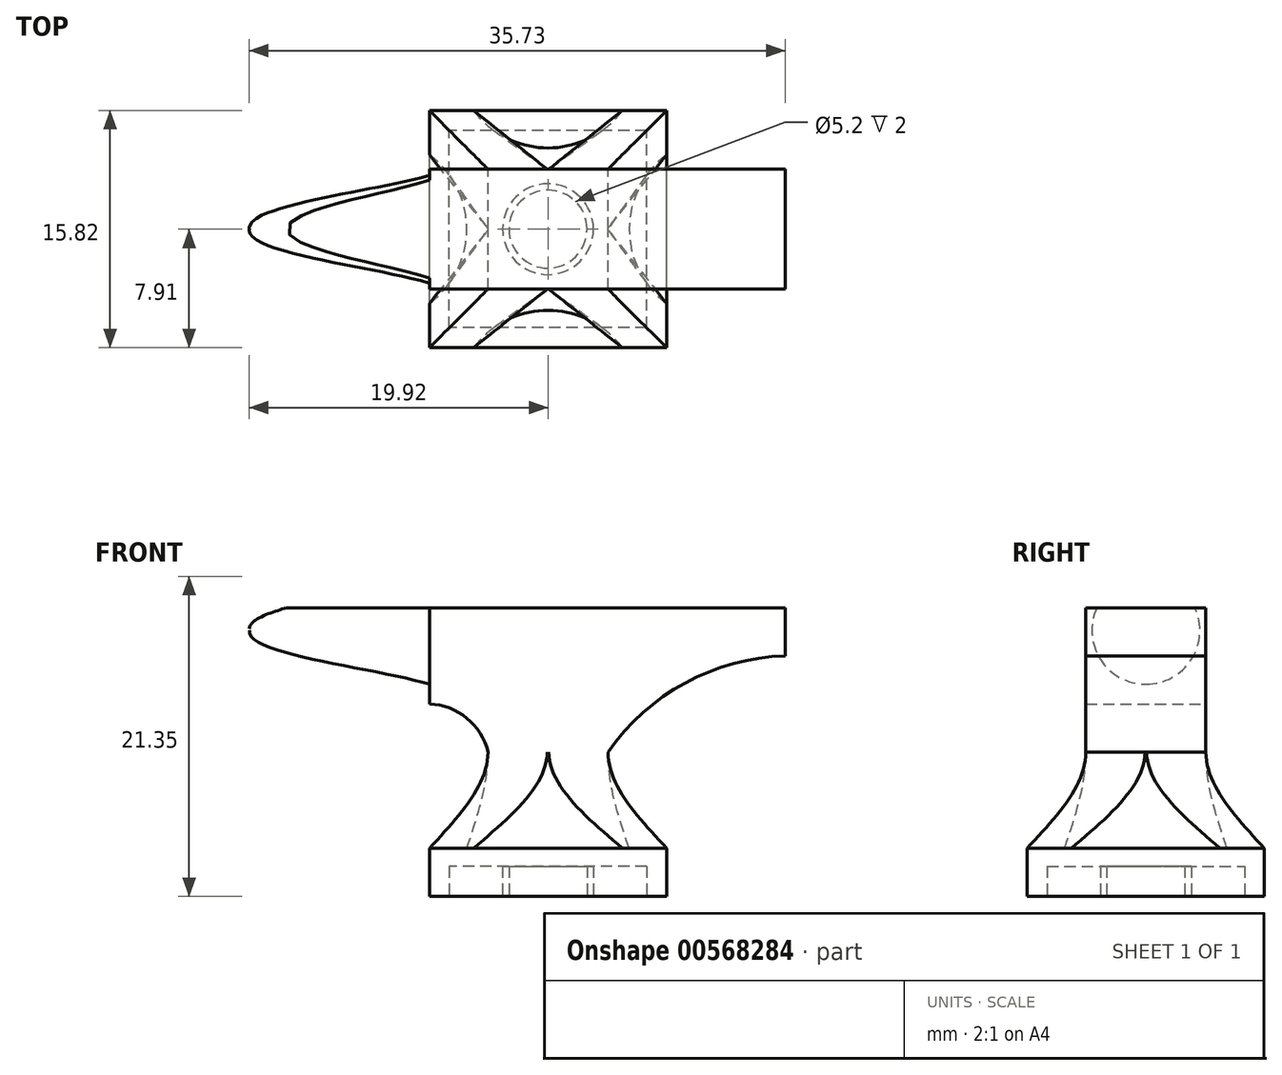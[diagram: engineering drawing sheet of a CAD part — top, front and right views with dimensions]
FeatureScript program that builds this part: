
annotation { "Feature Type Name" : "Feature", "Feature Type Description" : "" }
export const myFeature = defineFeature(function(context is Context, id is Id, definition is map)
    precondition{}
    {
        {
            assignVariable(context, id + "F0", {"name" : "lego_standard_width", "anyValue" : 15.8 / 2});
        }
        {
            assignVariable(context, id + "F1", {"name" : "base_width", "anyValue" : 8});
        }
        {
            var Q0;
            Q0=qCreatedBy(makeId("Front.planeOp"),FACE);
            var sketch = newSketch(context, id + "F2", { "sketchPlane" : qUnion([Q0])});
            skLineSegment(sketch, "E0", {"start": v(-7.9, 12.83) * mm, "end": v(-7.9, 19.25) * mm});
            skLineSegment(sketch, "E1", {"start": v(-7.9, 19.25) * mm, "end": v(15.8, 19.25) * mm});
            skLineSegment(sketch, "E2", {"start": v(15.8, 19.25) * mm, "end": v(15.8, 16.04) * mm});
            skLineSegment(sketch, "E3", {"start": v(-4, 9.62) * mm, "end": v(4, 9.62) * mm});
            skArc(sketch, "E4", {"start": v(-4, 9.62) * mm, "mid": v(-5.41, 11.89) * mm, "end": v(-7.9, 12.83) * mm});
            skArc(sketch, "E5", {"start": v(15.8, 16.04) * mm, "mid": v(9.14, 14.23) * mm, "end": v(4, 9.62) * mm});
            skLineSegment(sketch, "E6.bottom", {"start": v(7.9, 0) * mm, "end": v(-7.9, 0) * mm});
            skLineSegment(sketch, "E6.top", {"start": v(7.9, 3.21) * mm, "end": v(-7.9, 3.2) * mm});
            skLineSegment(sketch, "E6.left", {"start": v(7.9, 0) * mm, "end": v(7.9, 3.2) * mm});
            skLineSegment(sketch, "E6.right", {"start": v(-7.9, 0) * mm, "end": v(-7.9, 3.2) * mm});
            skPoint(sketch, "E6.middle", {"position": v(0, 1.6) * mm});
            skLineSegment(sketch, "E7", {"start": v(0, 3.2) * mm, "end": v(0, 9.62) * mm, "construction": true});
            skLineSegment(sketch, "E8", {"start": v(-7.9, 3.2) * mm, "end": v(-7.9, 12.83) * mm, "construction": true});
            skSolve(sketch);
        }
        {
            var Q0;
            Q0=makeQuery(id+"F2.imprint","IMPRINT",FACE,{"disambiguationData":[TD([[makeQuery(id+"F2.imprint","IMPRINT",EDGE,{"derivedFrom":sQuery(id+"F2.wireOp",EDGE,"E6.bottom")}),-1.0]])]});
            extrude(context, id + "F3", {"entities" : qUnion([Q0]), "depth" : getVariable(context, 'lego_standard_width') * mm, "offsetDistance" : 25 * mm, "hasSecondDirection" : true, "secondDirectionOppositeDirection" : true, "secondDirectionDepth" : getVariable(context, 'lego_standard_width') * mm});
        }
        {
            var Q0;
            Q0=makeQuery(id+"F2.imprint","IMPRINT",FACE,{"disambiguationData":[TD([[makeQuery(id+"F2.imprint","IMPRINT",EDGE,{"derivedFrom":sQuery(id+"F2.wireOp",EDGE,"E0")}),-1.0]])]});
            extrude(context, id + "F4", {"entities" : qUnion([Q0]), "depth" : getVariable(context, 'base_width') / 2 * mm, "offsetDistance" : 25 * mm, "hasSecondDirection" : true, "secondDirectionOppositeDirection" : true, "secondDirectionDepth" : getVariable(context, 'base_width') / 2 * mm});
        }
        {
            var Q0;
            Q0=makeQuery(id+"F3.opExtrude","SWEPT_FACE",FACE,{"disambiguationData":[OSD([sQuery(id+"F2.wireOp",EDGE,"E6.top")])]});
            var sketch = newSketch(context, id + "F5", { "sketchPlane" : qUnion([Q0])});
            skLineSegment(sketch, "E9", {"start": v(-7.9, 7.9) * mm, "end": v(7.9, -7.9) * mm, "construction": true});
            skLineSegment(sketch, "E10", {"start": v(-7.9, -7.9) * mm, "end": v(7.9, 7.9) * mm, "construction": true});
            skLineSegment(sketch, "E11", {"start": v(7.9, 7.9) * mm, "end": v(4.95, 7.9) * mm});
            skLineSegment(sketch, "E12", {"start": v(7.9, 7.9) * mm, "end": v(7.9, 4.95) * mm});
            skArc(sketch, "E13", {"start": v(7.9, 4.95) * mm, "mid": v(5.42, 0) * mm, "end": v(7.9, -4.95) * mm});
            skLineSegment(sketch, "E14.1.0", {"start": v(-7.9, 7.9) * mm, "end": v(-4.95, 7.9) * mm});
            skArc(sketch, "E14.1.1", {"start": v(-4.95, 7.9) * mm, "mid": v(0, 5.42) * mm, "end": v(4.95, 7.9) * mm});
            skLineSegment(sketch, "E14.1.2", {"start": v(-7.9, 7.9) * mm, "end": v(-7.9, 4.95) * mm});
            skLineSegment(sketch, "E14.2.0", {"start": v(-7.9, -7.9) * mm, "end": v(-7.9, -4.95) * mm});
            skArc(sketch, "E14.2.1", {"start": v(-7.9, -4.95) * mm, "mid": v(-5.42, 0) * mm, "end": v(-7.9, 4.95) * mm});
            skLineSegment(sketch, "E14.2.2", {"start": v(-7.9, -7.9) * mm, "end": v(-4.95, -7.9) * mm});
            skLineSegment(sketch, "E14.3.0", {"start": v(7.9, -7.9) * mm, "end": v(4.95, -7.9) * mm});
            skArc(sketch, "E14.3.1", {"start": v(4.95, -7.9) * mm, "mid": v(0, -5.42) * mm, "end": v(-4.95, -7.9) * mm});
            skLineSegment(sketch, "E14.3.2", {"start": v(7.9, -7.9) * mm, "end": v(7.9, -4.95) * mm});
            skPoint(sketch, "E14.center", {"position": v(0, 0) * mm});
            skSolve(sketch);
        }
        {
            var Q0;
            Q0=makeQuery(id+"F4.opExtrude","SWEPT_FACE",FACE,{"disambiguationData":[OSD([sQuery(id+"F2.wireOp",EDGE,"E3")])]});
            var sketch = newSketch(context, id + "F6", { "sketchPlane" : qUnion([Q0])});
            skLineSegment(sketch, "E15", {"start": v(-4, 4) * mm, "end": v(-0.05, 4) * mm});
            skLineSegment(sketch, "E16", {"start": v(-0.05, 4) * mm, "end": v(0.05, 4) * mm});
            skLineSegment(sketch, "E17", {"start": v(0.05, 4) * mm, "end": v(4, 4) * mm});
            skLineSegment(sketch, "E18", {"start": v(4, 4) * mm, "end": v(4, 0.05) * mm});
            skLineSegment(sketch, "E19", {"start": v(4, 0.05) * mm, "end": v(4, -0.05) * mm});
            skLineSegment(sketch, "E20", {"start": v(4, -0.05) * mm, "end": v(4, -4) * mm});
            skLineSegment(sketch, "E21", {"start": v(4, -4) * mm, "end": v(0.05, -4) * mm});
            skLineSegment(sketch, "E22", {"start": v(0.05, -4) * mm, "end": v(-0.05, -4) * mm});
            skLineSegment(sketch, "E23", {"start": v(-0.05, -4) * mm, "end": v(-4, -4) * mm});
            skLineSegment(sketch, "E24", {"start": v(-4, -4) * mm, "end": v(-4, -0.05) * mm});
            skLineSegment(sketch, "E25", {"start": v(-4, -0.05) * mm, "end": v(-4, 0.05) * mm});
            skLineSegment(sketch, "E26", {"start": v(-4, 0.05) * mm, "end": v(-4, 4) * mm});
            skPoint(sketch, "E27", {"position": v(0, 4) * mm});
            skSolve(sketch);
        }
        {
            var Q2;
            Q2=makeQuery(id+"F6.imprint","IMPRINT",FACE,{"disambiguationData":[TD([[makeQuery(id+"F6.imprint","IMPRINT",EDGE,{"derivedFrom":sQuery(id+"F6.wireOp",EDGE,"E15")}),-1.0]])]});
            var Q3;
            Q3=makeQuery(id+"F5.imprint","IMPRINT",FACE,{"disambiguationData":[TD([[makeQuery(id+"F5.imprint","IMPRINT",EDGE,{"derivedFrom":sQuery(id+"F5.wireOp",EDGE,"E11")}),1.0]])]});
            loft(context, id + "F7", {"operationType" : NewBodyOperationType.ADD, "startCondition" : LoftEndDerivativeType.NORMAL_TO_PROFILE, "startMagnitude" : 1, "sheetProfilesArray" : [{ "sheetProfileEntities" : qUnion([Q2]) }, { "sheetProfileEntities" : qUnion([Q3]) }]});
        }
        {
            var Q0;
            Q0=qCreatedBy(makeId("Front.planeOp"),FACE);
            var sketch = newSketch(context, id + "F8", { "sketchPlane" : qUnion([Q0])});
            skLineSegment(sketch, "E28.0", {"start": v(-7.9, 12.83) * mm, "end": v(-7.9, 19.25) * mm});
            skLineSegment(sketch, "E29", {"start": v(-7.9, 17.75) * mm, "end": v(-19.9, 17.75) * mm});
            skFitSpline(sketch, "E30", {"points": [v(-19.9, 17.75) * mm, v(-7.9, 14.15) * mm], "startDerivative": vector(-1.13, -4.8) * mm, "endDerivative": vector(10.6, -3.2) * mm});
            skSolve(sketch);
        }
        {
            var Q0;
            {var subQ0=sQuery(id+"F8.wireOp",EDGE,"E29");Q0=makeQuery(id+"F8.imprint","IMPRINT",FACE,{"disambiguationData":[TD([[makeQuery(id+"F8.imprint","IMPRINT",EDGE,{"derivedFrom":subQ0}),1.0]])]});}
            var Q1;
            Q1=sQuery(id+"F8.wireOp",EDGE,"E30");
            var Q2;
            Q2=sQuery(id+"F8.wireOp",EDGE,"E29");
            revolve(context, id + "F9", {"operationType" : NewBodyOperationType.ADD, "entities" : qUnion([Q0]), "surfaceEntities" : qUnion([Q1]), "axis" : qUnion([Q2]), "revolveType" : RevolveType.FULL});
        }
        {
            var Q0;
            Q0=makeQuery(id+"F9.opRevolve","SWEPT_FACE",FACE,{"disambiguationData":[OSD([sQuery(id+"F8.wireOp",EDGE,"E28.0")])]});
            extrude(context, id + "F10", {"entities" : qUnion([Q0]), "operationType" : NewBodyOperationType.REMOVE, "endBound" : BoundingType.THROUGH_ALL, "oppositeDirection" : true, "depth" : 25 * mm, "offsetDistance" : 25 * mm});
        }
        {
            var Q0;
            Q0=makeQuery(id+"F3.opExtrude","SWEPT_FACE",FACE,{"disambiguationData":[OSD([sQuery(id+"F2.wireOp",EDGE,"E6.bottom")])]});
            var sketch = newSketch(context, id + "F11", { "sketchPlane" : qUnion([Q0])});
            skLineSegment(sketch, "E31.0", {"start": v(6.58, 6.58) * mm, "end": v(-6.58, 6.58) * mm});
            skLineSegment(sketch, "E31.1", {"start": v(6.58, 6.58) * mm, "end": v(6.58, -6.58) * mm});
            skLineSegment(sketch, "E31.2", {"start": v(6.58, -6.58) * mm, "end": v(-6.58, -6.58) * mm});
            skLineSegment(sketch, "E31.3", {"start": v(-6.58, 6.58) * mm, "end": v(-6.58, -6.58) * mm});
            skCircle(sketch, "E32", {"center": v(0, 0) * mm, "radius": 3.03 * mm});
            skCircle(sketch, "E33", {"center": v(0, 0) * mm, "radius": 2.6 * mm});
            skCircle(sketch, "E34", {"center": v(-3.98, 3.98) * mm, "radius": 2.45 * mm, "construction": true});
            skCircle(sketch, "E35", {"center": v(3.98, 3.98) * mm, "radius": 2.45 * mm, "construction": true});
            skCircle(sketch, "E36", {"center": v(3.98, -3.98) * mm, "radius": 2.45 * mm, "construction": true});
            skCircle(sketch, "E37", {"center": v(-3.98, -3.98) * mm, "radius": 2.45 * mm, "construction": true});
            skLineSegment(sketch, "E38", {"start": v(-6.43, 6.43) * mm, "end": v(6.43, 6.43) * mm, "construction": true});
            skLineSegment(sketch, "E39", {"start": v(6.43, 6.43) * mm, "end": v(6.43, -6.43) * mm, "construction": true});
            skLineSegment(sketch, "E40", {"start": v(6.43, -6.43) * mm, "end": v(-6.43, -6.43) * mm, "construction": true});
            skLineSegment(sketch, "E41", {"start": v(-6.43, -6.43) * mm, "end": v(-6.43, 6.43) * mm, "construction": true});
            skLineSegment(sketch, "E42", {"start": v(-3.98, -3.98) * mm, "end": v(3.98, 3.98) * mm, "construction": true});
            skSolve(sketch);
        }
        {
            var Q0;
            Q0=makeQuery(id+"F11.imprint","IMPRINT",FACE,{"disambiguationData":[TD([[makeQuery(id+"F11.imprint","IMPRINT",EDGE,{"derivedFrom":sQuery(id+"F11.wireOp",EDGE,"E31.0")}),1.0]])]});
            var Q1;
            Q1=makeQuery(id+"F11.imprint","IMPRINT",FACE,{"disambiguationData":[TD([[makeQuery(id+"F11.imprint","IMPRINT",EDGE,{"derivedFrom":sQuery(id+"F11.wireOp",EDGE,"E33")}),1.0]])]});
            extrude(context, id + "F12", {"entities" : qUnion([Q0, Q1]), "operationType" : NewBodyOperationType.REMOVE, "oppositeDirection" : true, "depth" : 2 * mm, "offsetDistance" : 25 * mm});
        }
    });
